# Revit family: Strangregulierventil mit Messblende 4017 ML
name_source: partatom
category: Rohrzubehör
units: mm (PartAtom-declared; Revit-internal decimal feet)

## family parameters
Arbeitsebenenbasiert = Nein
Beim Laden mit Abzugskörper schneiden = Nein
Bemaßung runder Anschluss = Durchmesser verwenden
Gemeinsam genutzt = Nein
Immer vertikal = Ja
OmniClass-Nummer = 23.65.55.14
OmniClass-Titel = Valves for Liquid Services
Teiletyp = Unterbricht

## types (1)
- Strangregulierventil mit Messblende 4017 ML
    Anwendungsgebiet = Zum hydraulischen Abgleich in Heiz- oder Kühlanlagen, Einregulieren von Verteilleitungen, Strängen, Wärmetauschern,
Heiz- und Kühlregistern.
    Ausführung = STRÖMAX 4017 ML, Strangregulierventil mit Messblende und Impulsleitungsanschluss für Differenzdruckmessung in Schrägsitzform, mit Messventilen
Gelbe Ausführung aus entzinkungsbeständigen Messing, Muffe x Muffe, Spindelabdichtung mit Dreifach-O-Ring, Voreinstellung durch Hubbegrenzung, digitale Anzeige der Voreinstellstufe im Handradfenster.
    E00 = 0 mm  [stored 0 ft]
    Gehäuse = entzinkungsbeständigem Messing
    H02 = 13 mm
    Hersteller = HERZ Armaturen Ges.m.b.H.
    Max. Betriebsdruck = 2000000.0 Pa
    Max. Betriebstemperatur = 130 °C
    Max. Differenzdruck bei geschlossenen Sitz = 1000000.0 Pa
    Medium = Heizwasserqualität entsprechend ÖNORM H 5195 bzw. VDI-Richtlinie 2035
    R01 = 12 mm  [stored 0.0393701 ft]
    R02 = 9.5 mm  [stored 0.031168 ft]
    R03 = 21.5 mm
    S03 = 60 mm  [stored 0.19685 ft]
    SCRNCODE = 05;07;02
    SCRNSEQ = ARM;ARM_TYP="STRV";2
    SW01 = 60.00°
    URL = www.herz-armaturen.at
    W01 = 50.00°

note: [stored X ft] marks values corroborated as IEEE doubles in the binary element streams (Revit-internal decimal feet)

## geometry (parser evidence)
native form markers: Blend x1
no freeform markers — native parametric forms only
